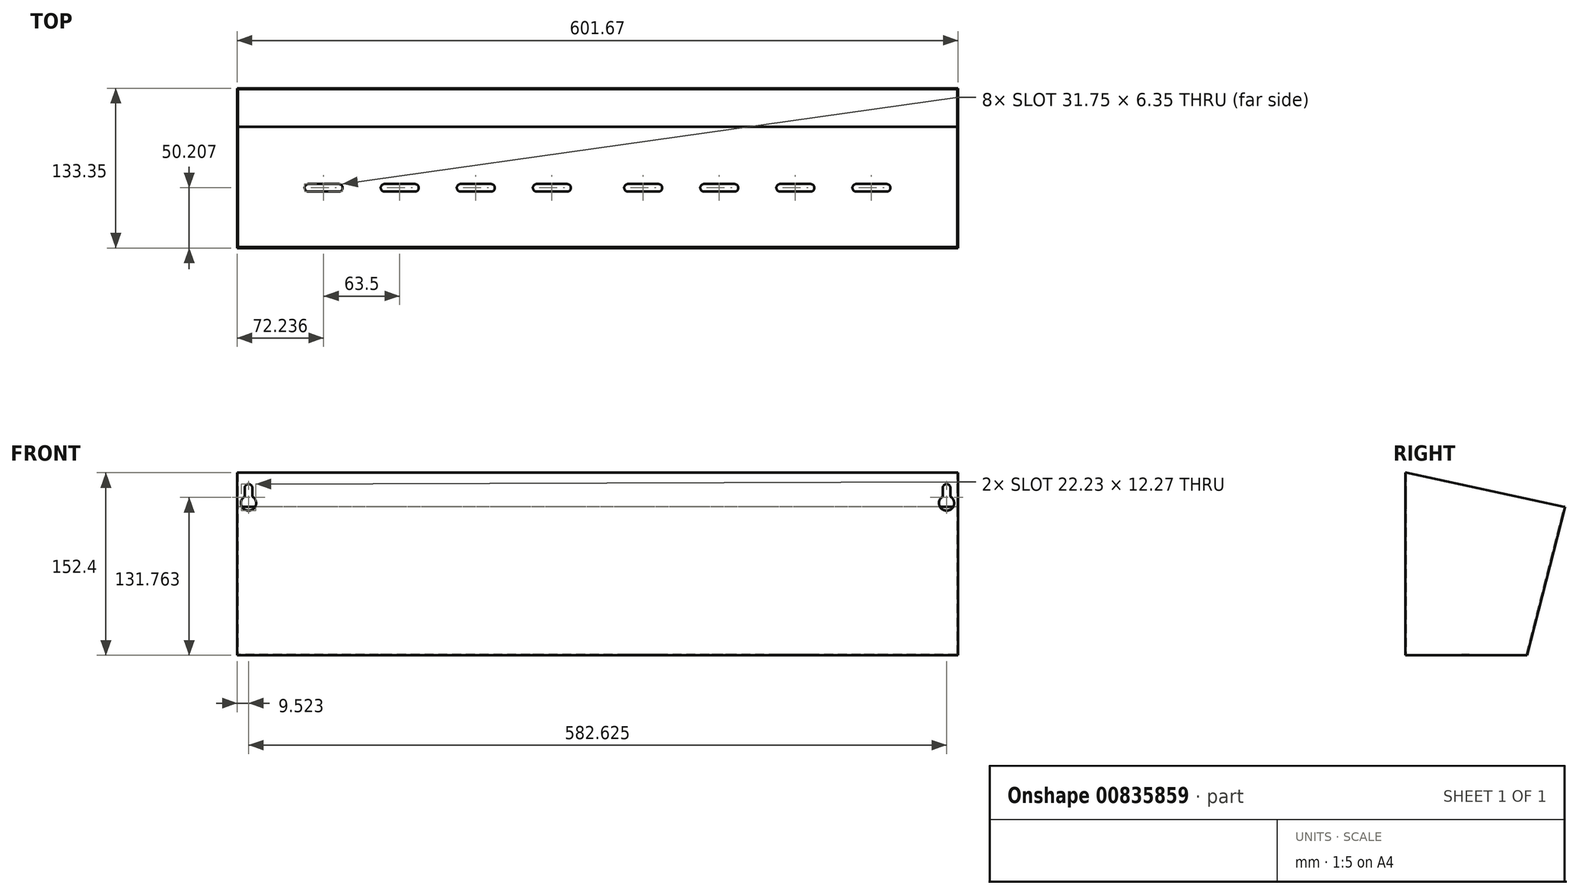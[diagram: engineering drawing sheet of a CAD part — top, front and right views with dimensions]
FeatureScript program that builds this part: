
annotation { "Feature Type Name" : "Feature", "Feature Type Description" : "" }
export const myFeature = defineFeature(function(context is Context, id is Id, definition is map)
    precondition{}
    {
        {
            var Q0;
            Q0=qCreatedBy(makeId("Right.planeOp"),FACE);
            var sketch = newSketch(context, id + "F0", { "sketchPlane" : qUnion([Q0])});
            skLineSegment(sketch, "E0", {"start": v(0, 0) * mm, "end": v(0, -151.64) * mm});
            skLineSegment(sketch, "E1", {"start": v(0, -151.64) * mm, "end": v(100.25, -151.64) * mm});
            skLineSegment(sketch, "E2", {"start": v(100.25, -151.64) * mm, "end": v(131.8, -28.62) * mm});
            skLineSegment(sketch, "E3.0", {"start": v(100.84, -152.4) * mm, "end": v(132.59, -28.62) * mm});
            skLineSegment(sketch, "E3.1", {"start": v(-0.76, -152.4) * mm, "end": v(100.84, -152.4) * mm});
            skLineSegment(sketch, "E3.2", {"start": v(-0.76, 0) * mm, "end": v(-0.76, -152.4) * mm});
            skLineSegment(sketch, "E4", {"start": v(131.8, -28.62) * mm, "end": v(132.59, -28.62) * mm});
            skLineSegment(sketch, "E5", {"start": v(-0.76, 0) * mm, "end": v(0, 0) * mm});
            skSolve(sketch);
        }
        {
            var Q0;
            Q0 = qSketchRegion(id + "F0", true);
            extrude(context, id + "F1", {"entities" : qUnion([Q0]), "depth" : 600.15 * mm, "offsetDistance" : 25.4 * mm});
        }
        {
            var Q0;
            Q0=makeQuery(id+"F1.opExtrude","CAP_FACE",FACE,{"disambiguationData":[OSD([sQuery(id+"F0.wireOp",EDGE,"E0"),sQuery(id+"F0.wireOp",EDGE,"E1"),sQuery(id+"F0.wireOp",EDGE,"E2"),sQuery(id+"F0.wireOp",EDGE,"E3.0"),sQuery(id+"F0.wireOp",EDGE,"E3.1"),sQuery(id+"F0.wireOp",EDGE,"E3.2"),sQuery(id+"F0.wireOp",EDGE,"E4"),sQuery(id+"F0.wireOp",EDGE,"E5")])],"isStart":false});
            var sketch = newSketch(context, id + "F2", { "sketchPlane" : qUnion([Q0])});
            skLineSegment(sketch, "E6", {"start": v(-0.76, 0) * mm, "end": v(-0.76, -152.4) * mm});
            skLineSegment(sketch, "E7", {"start": v(-0.76, -152.4) * mm, "end": v(100.84, -152.4) * mm});
            skLineSegment(sketch, "E8", {"start": v(100.84, -152.4) * mm, "end": v(132.59, -28.62) * mm});
            skLineSegment(sketch, "E9", {"start": v(132.59, -28.62) * mm, "end": v(131.8, -28.62) * mm});
            skLineSegment(sketch, "E10", {"start": v(131.8, -28.62) * mm, "end": v(0, 0) * mm});
            skLineSegment(sketch, "E11", {"start": v(0, 0) * mm, "end": v(-0.76, 0) * mm});
            skSolve(sketch);
        }
        {
            var Q0;
            Q0 = qSketchRegion(id + "F2", true);
            extrude(context, id + "F3", {"entities" : qUnion([Q0]), "operationType" : NewBodyOperationType.ADD, "depth" : 0.76 * mm, "offsetDistance" : 25.4 * mm});
        }
        {
            var Q0;
            Q0=makeQuery(id+"F1.opExtrude","CAP_FACE",FACE,{"disambiguationData":[OSD([sQuery(id+"F0.wireOp",EDGE,"E0"),sQuery(id+"F0.wireOp",EDGE,"E1"),sQuery(id+"F0.wireOp",EDGE,"E2"),sQuery(id+"F0.wireOp",EDGE,"E3.0"),sQuery(id+"F0.wireOp",EDGE,"E3.1"),sQuery(id+"F0.wireOp",EDGE,"E3.2"),sQuery(id+"F0.wireOp",EDGE,"E4"),sQuery(id+"F0.wireOp",EDGE,"E5")])],"isStart":true});
            var sketch = newSketch(context, id + "F4", { "sketchPlane" : qUnion([Q0])});
            skLineSegment(sketch, "E12", {"start": v(0.76, 0) * mm, "end": v(0, 0) * mm});
            skLineSegment(sketch, "E13", {"start": v(0, 0) * mm, "end": v(-131.8, -28.62) * mm});
            skLineSegment(sketch, "E14", {"start": v(-131.8, -28.62) * mm, "end": v(-132.59, -28.62) * mm});
            skLineSegment(sketch, "E15", {"start": v(-132.59, -28.62) * mm, "end": v(-100.84, -152.4) * mm});
            skLineSegment(sketch, "E16", {"start": v(-100.84, -152.4) * mm, "end": v(0.76, -152.4) * mm});
            skLineSegment(sketch, "E17", {"start": v(0.76, -152.4) * mm, "end": v(0.76, 0) * mm});
            skSolve(sketch);
        }
        {
            var Q0;
            Q0 = qSketchRegion(id + "F4", true);
            extrude(context, id + "F5", {"entities" : qUnion([Q0]), "operationType" : NewBodyOperationType.ADD, "depth" : 0.76 * mm, "offsetDistance" : 25.4 * mm});
        }
        {
            var Q0;
            Q0=makeQuery(id+"F5.boolean.opBoolean","MERGE",FACE,{"derivedFrom":[makeQuery(id+"F3.boolean.opBoolean","MERGE",FACE,{"derivedFrom":[makeQuery(id+"F1.opExtrude","SWEPT_FACE",FACE,{"disambiguationData":[OSD([sQuery(id+"F0.wireOp",EDGE,"E3.2")])]}),makeQuery(id+"F3.opExtrude","SWEPT_FACE",FACE,{"disambiguationData":[OSD([sQuery(id+"F2.wireOp",EDGE,"E6")])]})]}),makeQuery(id+"F5.opExtrude","SWEPT_FACE",FACE,{"disambiguationData":[OSD([sQuery(id+"F4.wireOp",EDGE,"E17")])]})]});
            var sketch = newSketch(context, id + "F6", { "sketchPlane" : qUnion([Q0])});
            skLineSegment(sketch, "E18", {"start": v(300.08, 0) * mm, "end": v(300.08, -152.4) * mm});
            skArc(sketch, "E19", {"start": v(5.59, -19.9) * mm, "mid": v(8.76, -31.75) * mm, "end": v(11.94, -19.9) * mm});
            skArc(sketch, "E20", {"start": v(11.94, -12.7) * mm, "mid": v(8.76, -9.53) * mm, "end": v(5.59, -12.7) * mm});
            skLineSegment(sketch, "E21", {"start": v(5.59, -12.7) * mm, "end": v(5.59, -19.9) * mm});
            skLineSegment(sketch, "E22", {"start": v(11.94, -12.7) * mm, "end": v(11.94, -19.9) * mm});
            skArc(sketch, "E23.MirrorCS", {"start": v(594.56, -19.9) * mm, "mid": v(591.39, -31.75) * mm, "end": v(588.21, -19.9) * mm});
            skLineSegment(sketch, "E24.MirrorCS", {"start": v(588.21, -12.7) * mm, "end": v(588.21, -19.9) * mm});
            skArc(sketch, "E25.MirrorCS", {"start": v(588.21, -12.7) * mm, "mid": v(591.39, -9.53) * mm, "end": v(594.56, -12.7) * mm});
            skLineSegment(sketch, "E26.MirrorCS", {"start": v(594.56, -12.7) * mm, "end": v(594.56, -19.9) * mm});
            skSolve(sketch);
        }
        {
            var Q0;
            Q0 = qSketchRegion(id + "F6", true);
            extrude(context, id + "F7", {"entities" : qUnion([Q0]), "operationType" : NewBodyOperationType.REMOVE, "oppositeDirection" : true, "depth" : 0.76 * mm, "offsetDistance" : 25.4 * mm});
        }
        {
            var Q0;
            Q0=makeQuery(id+"F1.opExtrude","SWEPT_FACE",FACE,{"disambiguationData":[OSD([sQuery(id+"F0.wireOp",EDGE,"E1")])]});
            var sketch = newSketch(context, id + "F8", { "sketchPlane" : qUnion([Q0])});
            skLineSegment(sketch, "E27.bottom", {"start": v(58.78, 52.62) * mm, "end": v(84.18, 52.62) * mm});
            skLineSegment(sketch, "E27.top", {"start": v(58.78, 46.27) * mm, "end": v(84.18, 46.27) * mm});
            skLineSegment(sketch, "E28", {"start": v(300.08, 100.25) * mm, "end": v(300.08, 0) * mm});
            skArc(sketch, "E29", {"start": v(84.18, 46.27) * mm, "mid": v(87.35, 49.45) * mm, "end": v(84.18, 52.62) * mm});
            skArc(sketch, "E30", {"start": v(58.78, 52.62) * mm, "mid": v(55.6, 49.45) * mm, "end": v(58.78, 46.27) * mm});
            skLineSegment(sketch, "E31.bottom", {"start": v(122.28, 52.62) * mm, "end": v(147.68, 52.62) * mm});
            skLineSegment(sketch, "E31.top", {"start": v(122.28, 46.27) * mm, "end": v(147.68, 46.27) * mm});
            skArc(sketch, "E32", {"start": v(147.68, 46.27) * mm, "mid": v(150.85, 49.45) * mm, "end": v(147.68, 52.62) * mm});
            skArc(sketch, "E33", {"start": v(122.28, 52.62) * mm, "mid": v(119.1, 49.45) * mm, "end": v(122.28, 46.27) * mm});
            skLineSegment(sketch, "E34.bottom", {"start": v(185.78, 52.62) * mm, "end": v(211.18, 52.62) * mm});
            skLineSegment(sketch, "E34.top", {"start": v(185.78, 46.27) * mm, "end": v(211.18, 46.27) * mm});
            skArc(sketch, "E35", {"start": v(211.18, 46.27) * mm, "mid": v(214.35, 49.45) * mm, "end": v(211.18, 52.62) * mm});
            skArc(sketch, "E36", {"start": v(185.78, 52.62) * mm, "mid": v(182.6, 49.45) * mm, "end": v(185.78, 46.27) * mm});
            skLineSegment(sketch, "E37.bottom", {"start": v(249.28, 52.62) * mm, "end": v(274.68, 52.62) * mm});
            skLineSegment(sketch, "E37.top", {"start": v(249.28, 46.27) * mm, "end": v(274.68, 46.27) * mm});
            skArc(sketch, "E38", {"start": v(274.68, 46.27) * mm, "mid": v(277.85, 49.45) * mm, "end": v(274.68, 52.62) * mm});
            skArc(sketch, "E39", {"start": v(249.28, 52.62) * mm, "mid": v(246.1, 49.45) * mm, "end": v(249.28, 46.27) * mm});
            skLineSegment(sketch, "E40.MirrorCS", {"start": v(350.88, 52.62) * mm, "end": v(325.48, 52.62) * mm});
            skArc(sketch, "E41.MirrorCS", {"start": v(325.48, 46.27) * mm, "mid": v(322.3, 49.45) * mm, "end": v(325.48, 52.62) * mm});
            skLineSegment(sketch, "E42.MirrorCS", {"start": v(350.88, 46.27) * mm, "end": v(325.48, 46.27) * mm});
            skArc(sketch, "E43.MirrorCS", {"start": v(350.88, 52.62) * mm, "mid": v(354.05, 49.45) * mm, "end": v(350.88, 46.27) * mm});
            skArc(sketch, "E44.MirrorCS", {"start": v(388.98, 46.27) * mm, "mid": v(385.8, 49.45) * mm, "end": v(388.98, 52.62) * mm});
            skLineSegment(sketch, "E45.MirrorCS", {"start": v(414.38, 52.62) * mm, "end": v(388.98, 52.62) * mm});
            skLineSegment(sketch, "E46.MirrorCS", {"start": v(414.38, 46.27) * mm, "end": v(388.98, 46.27) * mm});
            skArc(sketch, "E47.MirrorCS", {"start": v(414.38, 52.62) * mm, "mid": v(417.55, 49.45) * mm, "end": v(414.38, 46.27) * mm});
            skArc(sketch, "E48.MirrorCS", {"start": v(452.48, 46.27) * mm, "mid": v(449.3, 49.45) * mm, "end": v(452.48, 52.62) * mm});
            skLineSegment(sketch, "E49.MirrorCS", {"start": v(477.88, 46.27) * mm, "end": v(452.48, 46.27) * mm});
            skLineSegment(sketch, "E50.MirrorCS", {"start": v(477.88, 52.62) * mm, "end": v(452.48, 52.62) * mm});
            skArc(sketch, "E51.MirrorCS", {"start": v(477.88, 52.62) * mm, "mid": v(481.05, 49.45) * mm, "end": v(477.88, 46.27) * mm});
            skArc(sketch, "E52.MirrorCS", {"start": v(541.38, 52.62) * mm, "mid": v(544.55, 49.45) * mm, "end": v(541.38, 46.27) * mm});
            skLineSegment(sketch, "E53.MirrorCS", {"start": v(541.38, 52.62) * mm, "end": v(515.98, 52.62) * mm});
            skLineSegment(sketch, "E54.MirrorCS", {"start": v(541.38, 46.27) * mm, "end": v(515.98, 46.27) * mm});
            skArc(sketch, "E55.MirrorCS", {"start": v(515.98, 46.27) * mm, "mid": v(512.8, 49.45) * mm, "end": v(515.98, 52.62) * mm});
            skSolve(sketch);
        }
        {
            var Q0;
            Q0 = qSketchRegion(id + "F8", true);
            extrude(context, id + "F9", {"entities" : qUnion([Q0]), "operationType" : NewBodyOperationType.REMOVE, "oppositeDirection" : true, "depth" : 25.4 * mm, "offsetDistance" : 25.4 * mm});
        }
    });
